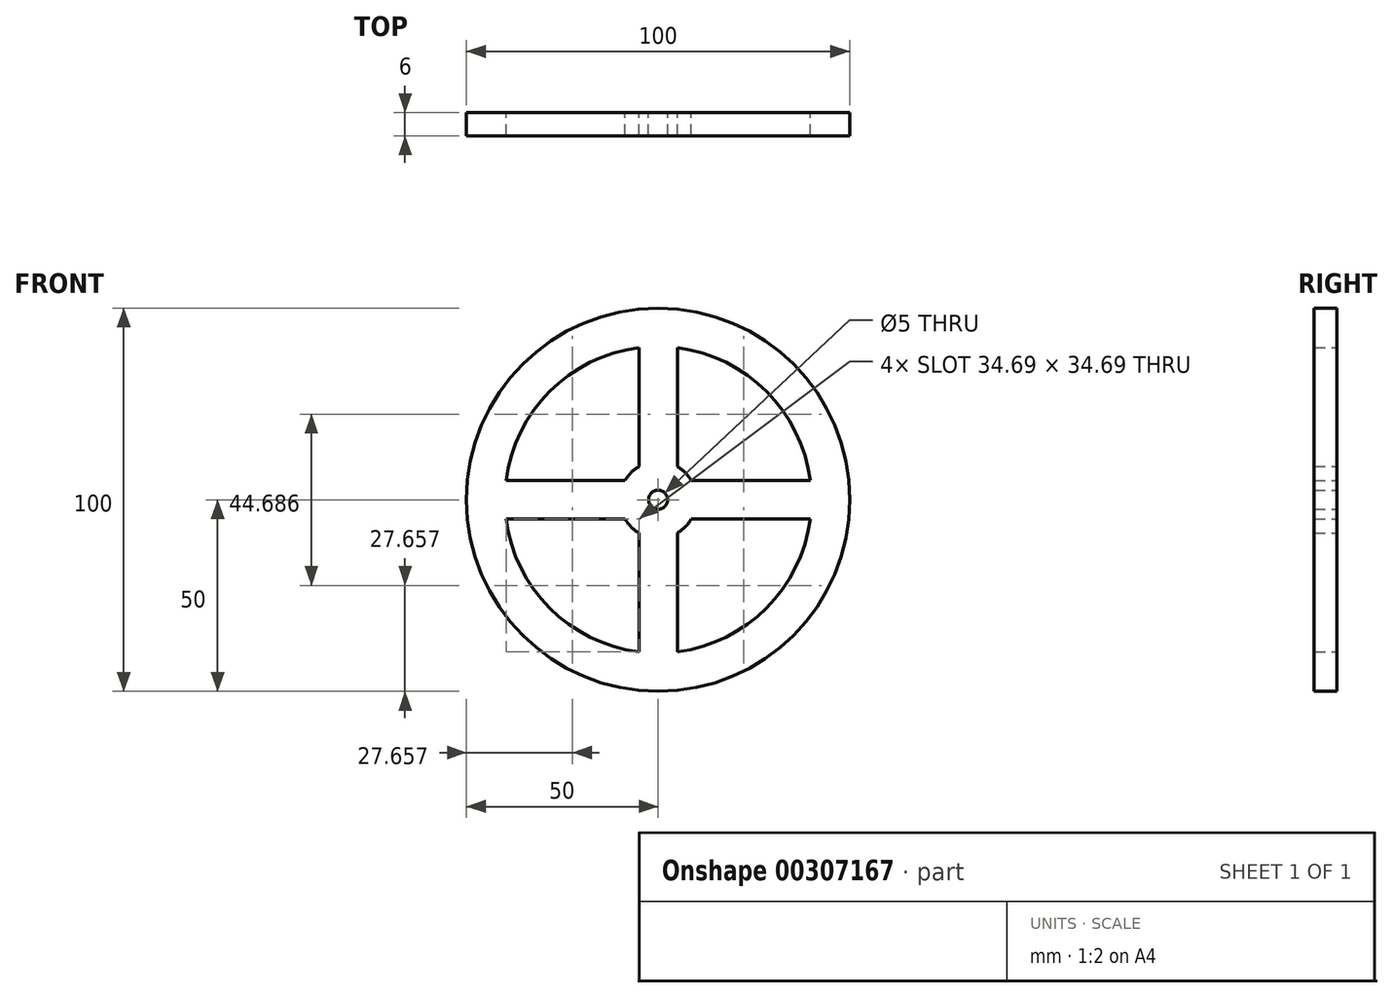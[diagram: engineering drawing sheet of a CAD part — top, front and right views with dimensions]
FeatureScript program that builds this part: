
annotation { "Feature Type Name" : "Feature", "Feature Type Description" : "" }
export const myFeature = defineFeature(function(context is Context, id is Id, definition is map)
    precondition{}
    {
        {
            var Q0;
            Q0=qCreatedBy(makeId("Front.planeOp"),FACE);
            var sketch = newSketch(context, id + "F0", { "sketchPlane" : qUnion([Q0])});
            skCircle(sketch, "E0", {"center": v(0, 0) * mm, "radius": 50 * mm});
            skArc(sketch, "E1", {"start": v(-39.69, -5) * mm, "mid": v(-28.28, -28.28) * mm, "end": v(-5, -39.69) * mm});
            skArc(sketch, "E2", {"start": v(5, -8.66) * mm, "mid": v(7.07, -7.07) * mm, "end": v(8.66, -5) * mm});
            skCircle(sketch, "E3", {"center": v(0, 0) * mm, "radius": 2.5 * mm});
            skLineSegment(sketch, "E4", {"start": v(0, 0) * mm, "end": v(0, 50) * mm, "construction": true});
            skLineSegment(sketch, "E5", {"start": v(0, 0) * mm, "end": v(50, 0) * mm, "construction": true});
            skLineSegment(sketch, "E6", {"start": v(0, 0) * mm, "end": v(-50, 0) * mm, "construction": true});
            skLineSegment(sketch, "E7", {"start": v(0, 0) * mm, "end": v(0, -50) * mm, "construction": true});
            skLineSegment(sketch, "E8.0", {"start": v(-5, -8.66) * mm, "end": v(-5, -39.69) * mm});
            skLineSegment(sketch, "E9.0", {"start": v(-8.66, -5) * mm, "end": v(-39.69, -5) * mm});
            skArc(sketch, "E10.trimOffspring", {"start": v(-5, 39.69) * mm, "mid": v(-28.28, 28.28) * mm, "end": v(-39.69, 5) * mm});
            skArc(sketch, "E11.trimOffspring", {"start": v(39.69, 5) * mm, "mid": v(28.28, 28.28) * mm, "end": v(5, 39.69) * mm});
            skArc(sketch, "E12.trimOffspring", {"start": v(5, -39.69) * mm, "mid": v(28.28, -28.28) * mm, "end": v(39.69, -5) * mm});
            skArc(sketch, "E13.trimOffspring", {"start": v(-5, 8.66) * mm, "mid": v(-7.07, 7.07) * mm, "end": v(-8.66, 5) * mm});
            skArc(sketch, "E14.trimOffspring", {"start": v(-8.66, -5) * mm, "mid": v(-7.07, -7.07) * mm, "end": v(-5, -8.66) * mm});
            skLineSegment(sketch, "E15.trimOffspring", {"start": v(-8.66, 5) * mm, "end": v(-39.69, 5) * mm});
            skLineSegment(sketch, "E16.trimOffspring", {"start": v(-5, 8.66) * mm, "end": v(-5, 39.69) * mm});
            skLineSegment(sketch, "E17.trimOffspring", {"start": v(5, 8.66) * mm, "end": v(5, 39.69) * mm});
            skLineSegment(sketch, "E18.trimOffspring", {"start": v(8.66, 5) * mm, "end": v(39.69, 5) * mm});
            skLineSegment(sketch, "E19.trimOffspring", {"start": v(8.66, -5) * mm, "end": v(39.69, -5) * mm});
            skLineSegment(sketch, "E20.trimOffspring", {"start": v(5, -8.66) * mm, "end": v(5, -39.69) * mm});
            skArc(sketch, "E21.trimOffspring", {"start": v(8.66, 5) * mm, "mid": v(7.07, 7.07) * mm, "end": v(5, 8.66) * mm});
            skSolve(sketch);
        }
        {
            var Q0;
            Q0=makeQuery(id+"F0.imprint","IMPRINT",FACE,{"disambiguationData":[TD([[makeQuery(id+"F0.imprint","IMPRINT",EDGE,{"derivedFrom":sQuery(id+"F0.wireOp",EDGE,"E0")}),1.0]])]});
            extrude(context, id + "F1", {"entities" : qUnion([Q0]), "endBound" : BoundingType.SYMMETRIC, "depth" : 6 * mm});
        }
    });
